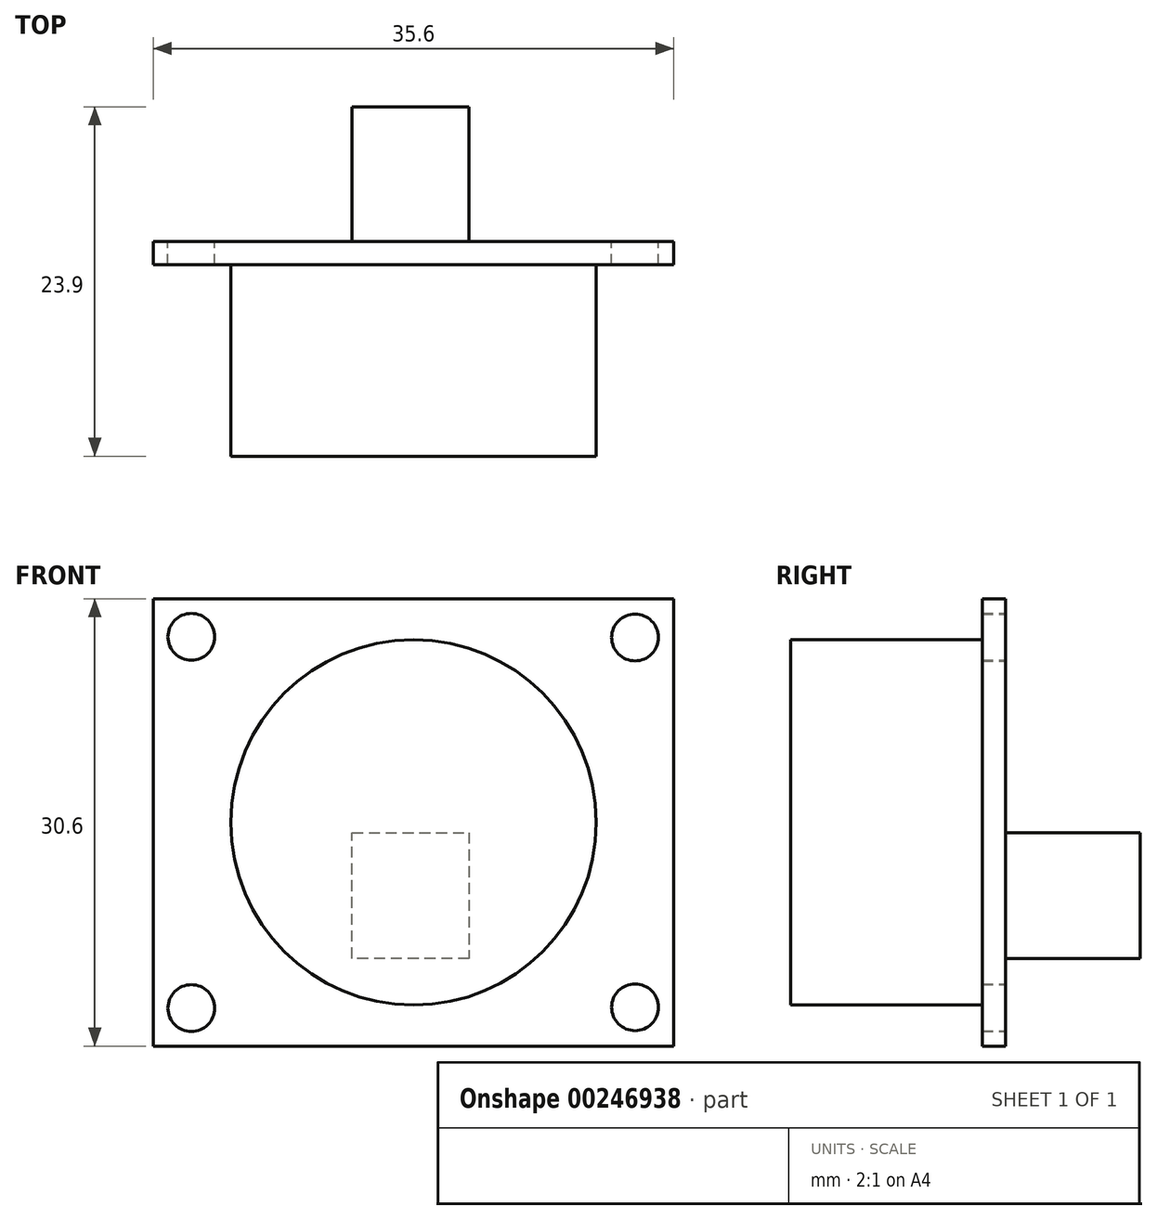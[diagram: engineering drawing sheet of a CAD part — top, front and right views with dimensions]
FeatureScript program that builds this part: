
annotation { "Feature Type Name" : "Feature", "Feature Type Description" : "" }
export const myFeature = defineFeature(function(context is Context, id is Id, definition is map)
    precondition{}
    {
        {
            var Q0;
            Q0=qCreatedBy(makeId("Front.planeOp"),FACE);
            var sketch = newSketch(context, id + "F0", { "sketchPlane" : qUnion([Q0])});
            skLineSegment(sketch, "E0", {"start": v(-17.8, 15.3) * mm, "end": v(-17.8, -15.3) * mm});
            skLineSegment(sketch, "E1", {"start": v(-17.8, -15.3) * mm, "end": v(17.8, -15.3) * mm});
            skLineSegment(sketch, "E2", {"start": v(17.8, -15.3) * mm, "end": v(17.8, 15.3) * mm});
            skLineSegment(sketch, "E3", {"start": v(17.8, 15.3) * mm, "end": v(-17.8, 15.3) * mm});
            skLineSegment(sketch, "E4", {"start": v(-17.8, -15.3) * mm, "end": v(17.8, 15.3) * mm, "construction": true});
            skLineSegment(sketch, "E5", {"start": v(17.8, -15.3) * mm, "end": v(-17.8, 15.3) * mm, "construction": true});
            skPoint(sketch, "E6", {"position": v(0, 0) * mm});
            skLineSegment(sketch, "E7", {"start": v(17.8, 15.3) * mm, "end": v(17.8, 12.65) * mm, "construction": true});
            skLineSegment(sketch, "E8", {"start": v(17.8, 12.65) * mm, "end": v(15.15, 12.65) * mm, "construction": true});
            skLineSegment(sketch, "E9", {"start": v(-17.8, 15.3) * mm, "end": v(-17.8, 12.7) * mm, "construction": true});
            skLineSegment(sketch, "E10", {"start": v(-17.8, 12.7) * mm, "end": v(-15.2, 12.7) * mm, "construction": true});
            skLineSegment(sketch, "E11", {"start": v(-17.8, -15.3) * mm, "end": v(-15.2, -15.3) * mm, "construction": true});
            skLineSegment(sketch, "E12", {"start": v(-15.2, -15.3) * mm, "end": v(-15.2, -12.7) * mm, "construction": true});
            skLineSegment(sketch, "E13", {"start": v(17.8, -15.3) * mm, "end": v(15.15, -15.3) * mm, "construction": true});
            skLineSegment(sketch, "E14", {"start": v(15.15, -15.3) * mm, "end": v(15.15, -12.65) * mm, "construction": true});
            skCircle(sketch, "E15", {"center": v(15.15, -12.65) * mm, "radius": 1.6 * mm});
            skCircle(sketch, "E16", {"center": v(15.15, 12.65) * mm, "radius": 1.6 * mm});
            skCircle(sketch, "E17", {"center": v(-15.2, 12.7) * mm, "radius": 1.6 * mm});
            skCircle(sketch, "E18", {"center": v(-15.2, -12.7) * mm, "radius": 1.6 * mm});
            skSolve(sketch);
        }
        {
            var Q0;
            Q0=makeQuery(id+"F0.imprint","IMPRINT",FACE,{"disambiguationData":[TD([[makeQuery(id+"F0.imprint","IMPRINT",EDGE,{"derivedFrom":sQuery(id+"F0.wireOp",EDGE,"E0")}),1.0]])]});
            extrude(context, id + "F1", {"entities" : qUnion([Q0]), "depth" : 1.6 * mm});
        }
        {
            var Q0;
            Q0=makeQuery(id+"F1.opExtrude","CAP_FACE",FACE,{"disambiguationData":[OSD([sQuery(id+"F0.wireOp",EDGE,"E0"),sQuery(id+"F0.wireOp",EDGE,"E1"),sQuery(id+"F0.wireOp",EDGE,"E2"),sQuery(id+"F0.wireOp",EDGE,"E3"),sQuery(id+"F0.wireOp",EDGE,"E15"),sQuery(id+"F0.wireOp",EDGE,"E16"),sQuery(id+"F0.wireOp",EDGE,"E17"),sQuery(id+"F0.wireOp",EDGE,"E18")])],"isStart":false});
            var sketch = newSketch(context, id + "F2", { "sketchPlane" : qUnion([Q0])});
            skCircle(sketch, "E19", {"center": v(0, 0) * mm, "radius": 12.5 * mm});
            skSolve(sketch);
        }
        {
            var Q0;
            Q0=makeQuery(id+"F2.imprint","IMPRINT",FACE,{"disambiguationData":[TD([[makeQuery(id+"F2.imprint","IMPRINT",EDGE,{"derivedFrom":sQuery(id+"F2.wireOp",EDGE,"E19")}),1.0]])]});
            extrude(context, id + "F3", {"entities" : qUnion([Q0]), "operationType" : NewBodyOperationType.ADD, "depth" : 13.1 * mm});
        }
        {
            var Q0;
            Q0=makeQuery(id+"F1.opExtrude","CAP_FACE",FACE,{"disambiguationData":[OSD([sQuery(id+"F0.wireOp",EDGE,"E0"),sQuery(id+"F0.wireOp",EDGE,"E1"),sQuery(id+"F0.wireOp",EDGE,"E2"),sQuery(id+"F0.wireOp",EDGE,"E3"),sQuery(id+"F0.wireOp",EDGE,"E15"),sQuery(id+"F0.wireOp",EDGE,"E16"),sQuery(id+"F0.wireOp",EDGE,"E17"),sQuery(id+"F0.wireOp",EDGE,"E18")])],"isStart":true});
            var sketch = newSketch(context, id + "F4", { "sketchPlane" : qUnion([Q0])});
            skLineSegment(sketch, "E20", {"start": v(-17.8, -15.3) * mm, "end": v(-3.8, -15.3) * mm, "construction": true});
            skLineSegment(sketch, "E21", {"start": v(-3.8, -15.3) * mm, "end": v(-3.8, -9.3) * mm, "construction": true});
            skLineSegment(sketch, "E22", {"start": v(-3.8, -9.3) * mm, "end": v(4.2, -9.3) * mm});
            skLineSegment(sketch, "E23", {"start": v(4.2, -9.3) * mm, "end": v(4.2, -0.7) * mm});
            skLineSegment(sketch, "E24", {"start": v(4.2, -0.7) * mm, "end": v(-3.8, -0.7) * mm});
            skLineSegment(sketch, "E25", {"start": v(-3.8, -0.7) * mm, "end": v(-3.8, -9.3) * mm});
            skSolve(sketch);
        }
        {
            var Q0;
            Q0=makeQuery(id+"F4.imprint","IMPRINT",FACE,{"disambiguationData":[TD([[makeQuery(id+"F4.imprint","IMPRINT",EDGE,{"derivedFrom":sQuery(id+"F4.wireOp",EDGE,"E22")}),1.0]])]});
            extrude(context, id + "F5", {"entities" : qUnion([Q0]), "operationType" : NewBodyOperationType.ADD, "depth" : 9.2 * mm});
        }
    });
